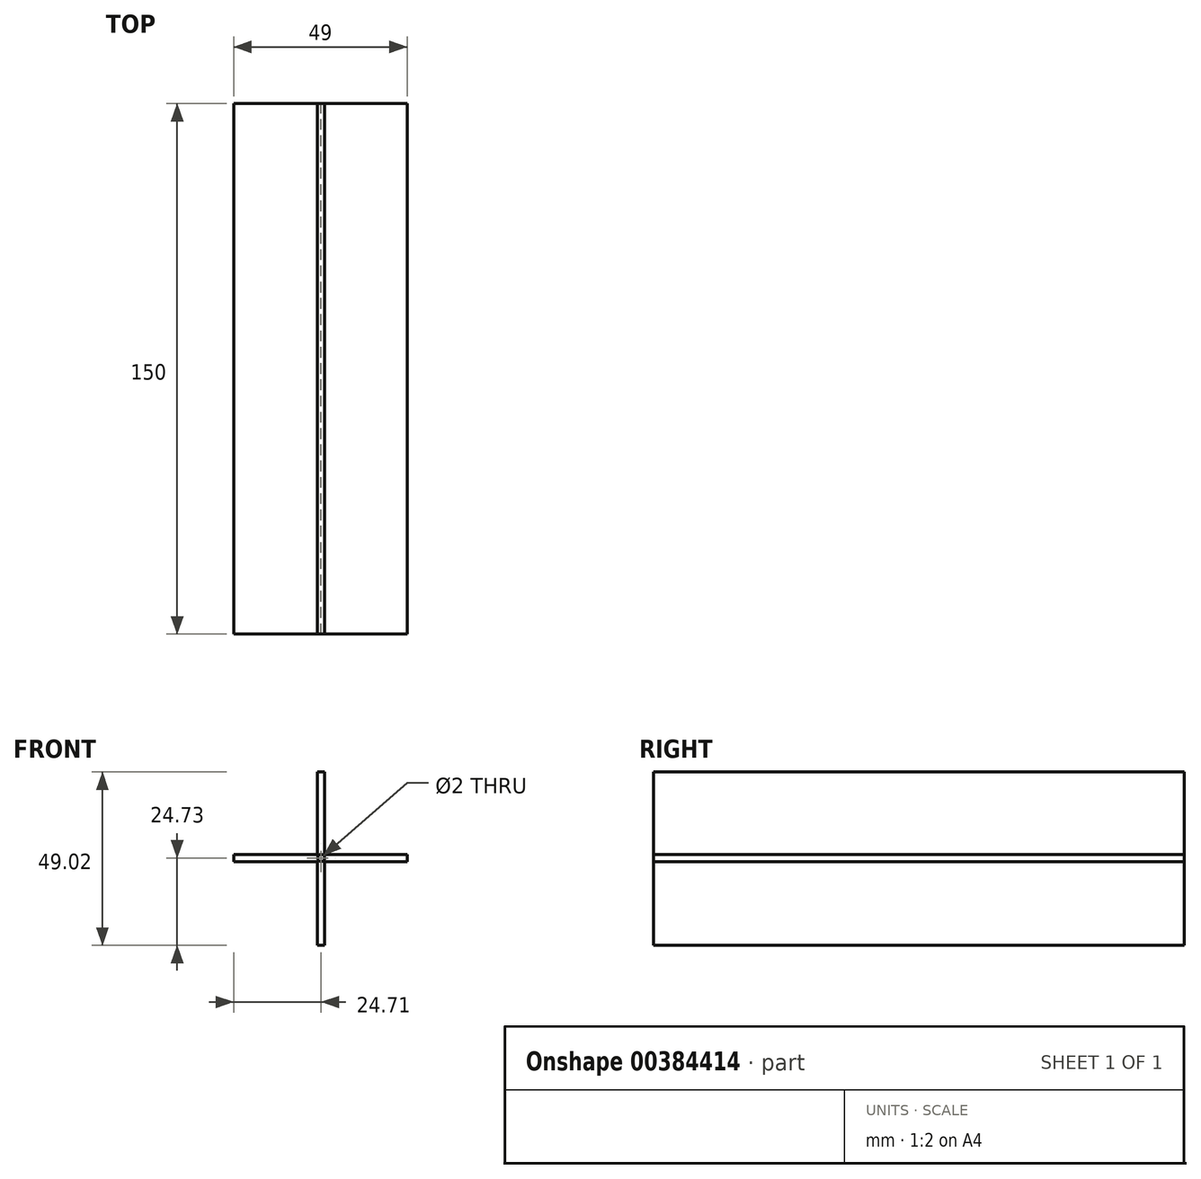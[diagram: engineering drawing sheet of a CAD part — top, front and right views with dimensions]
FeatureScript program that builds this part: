
annotation { "Feature Type Name" : "Feature", "Feature Type Description" : "" }
export const myFeature = defineFeature(function(context is Context, id is Id, definition is map)
    precondition{}
    {
        {
            var Q0;
            Q0=qCreatedBy(makeId("Front.planeOp"),FACE);
            var sketch = newSketch(context, id + "F0", { "sketchPlane" : qUnion([Q0])});
            skLineSegment(sketch, "E0", {"start": v(0, -24.71) * mm, "end": v(0, 24.71) * mm});
            skLineSegment(sketch, "E1", {"start": v(-24.71, 0) * mm, "end": v(24.29, 0) * mm});
            skPoint(sketch, "E2.center.orphan", {"position": v(0, 0) * mm});
            skLineSegment(sketch, "E3", {"start": v(-24.71, 0) * mm, "end": v(-24.71, -1) * mm});
            skLineSegment(sketch, "E4", {"start": v(-24.71, -1) * mm, "end": v(24.29, -1) * mm});
            skLineSegment(sketch, "E5", {"start": v(0, -24.71) * mm, "end": v(-1, -24.73) * mm});
            skLineSegment(sketch, "E6", {"start": v(-1, -24.73) * mm, "end": v(-1, 24.29) * mm});
            skLineSegment(sketch, "E7", {"start": v(-1, 24.29) * mm, "end": v(1, 24.29) * mm});
            skLineSegment(sketch, "E8", {"start": v(1, 24.29) * mm, "end": v(1, -24.71) * mm});
            skLineSegment(sketch, "E9", {"start": v(1, -24.71) * mm, "end": v(0, -24.71) * mm});
            skLineSegment(sketch, "E10", {"start": v(24.29, 0) * mm, "end": v(24.29, -1) * mm});
            skLineSegment(sketch, "E11", {"start": v(-24.71, 0) * mm, "end": v(-24.71, 1) * mm});
            skLineSegment(sketch, "E12", {"start": v(-24.71, 1) * mm, "end": v(24.29, 1) * mm});
            skLineSegment(sketch, "E13", {"start": v(24.29, 1) * mm, "end": v(24.29, 0) * mm});
            skCircle(sketch, "E14", {"center": v(0, 0) * mm, "radius": 1 * mm});
            skSolve(sketch);
        }
        {
            var Q0;
            Q0 = qSketchRegion(id + "F0", true);
            extrude(context, id + "F1", {"entities" : qUnion([Q0]), "depth" : 150 * mm});
        }
    });
